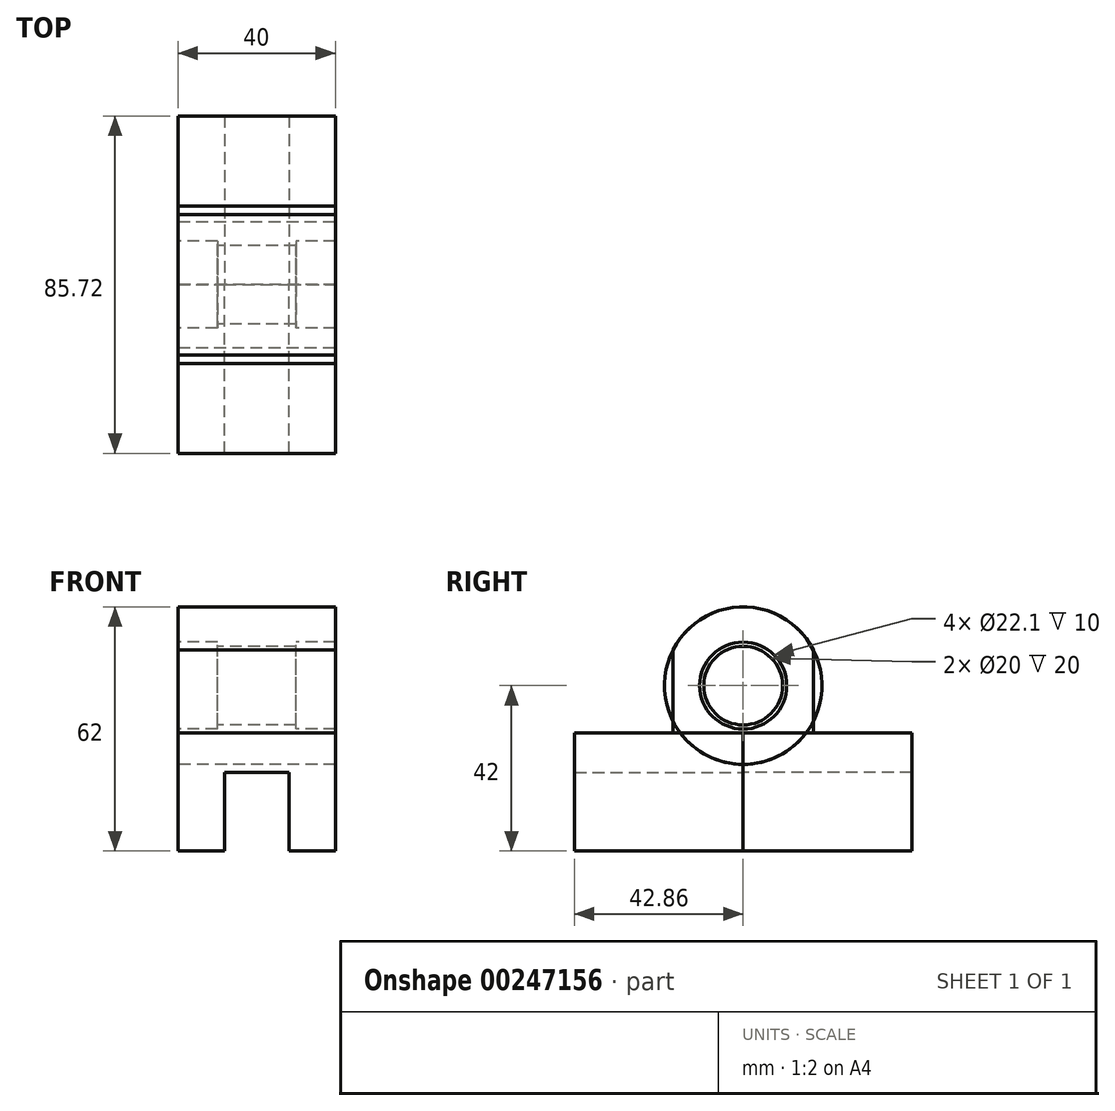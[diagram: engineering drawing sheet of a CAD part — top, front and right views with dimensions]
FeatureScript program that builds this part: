
annotation { "Feature Type Name" : "Feature", "Feature Type Description" : "" }
export const myFeature = defineFeature(function(context is Context, id is Id, definition is map)
    precondition{}
    {
        {
            var Q0;
            Q0=qCreatedBy(makeId("Right.planeOp"),FACE);
            var sketch = newSketch(context, id + "F0", { "sketchPlane" : qUnion([Q0])});
            skCircle(sketch, "E0", {"center": v(0, 0) * mm, "radius": 11.05 * mm});
            skCircle(sketch, "E1", {"center": v(0, 0) * mm, "radius": 20 * mm});
            skCircle(sketch, "E2", {"center": v(0, 0) * mm, "radius": 10 * mm});
            skLineSegment(sketch, "E3.bottom", {"start": v(-17.86, 9) * mm, "end": v(-42.86, 9) * mm});
            skLineSegment(sketch, "E3.top", {"start": v(-17.86, -12) * mm, "end": v(-42.86, -12) * mm});
            skLineSegment(sketch, "E3.left", {"start": v(-17.86, 9) * mm, "end": v(-17.86, -12) * mm});
            skLineSegment(sketch, "E3.right", {"start": v(-42.86, 9) * mm, "end": v(-42.86, -12) * mm});
            skCircle(sketch, "E4", {"center": v(-32.86, 0) * mm, "radius": 3.15 * mm});
            skLineSegment(sketch, "E5.bottom", {"start": v(-42.86, -12) * mm, "end": v(0, -12) * mm});
            skLineSegment(sketch, "E5.top", {"start": v(-42.86, -42) * mm, "end": v(0, -42) * mm});
            skLineSegment(sketch, "E5.left", {"start": v(-42.86, -12) * mm, "end": v(-42.86, -42) * mm});
            skLineSegment(sketch, "E5.right", {"start": v(0, -12) * mm, "end": v(0, -42) * mm});
            skSolve(sketch);
        }
        {
            var Q0;
            Q0=makeQuery(id+"F0.imprint","IMPRINT",FACE,{"disambiguationData":[TD([[makeQuery(id+"F0.imprint","IMPRINT",EDGE,{"derivedFrom":sQuery(id+"F0.wireOp",EDGE,"E0")}),-1.0]])]});
            var Q1;
            {var subQ0=sQuery(id+"F0.wireOp",EDGE,"E5.bottom");var subQ1=sQuery(id+"F0.wireOp",EDGE,"E1");var subQ2=makeQuery(id+"F0.imprint","INTERSECT",VERTEX,{"derivedFrom":[subQ1,subQ0]});Q1=makeQuery(id+"F0.imprint","IMPRINT",FACE,{"disambiguationData":[TD([[makeQuery(id+"F0.imprint","IMPRINT",EDGE,{"disambiguationData":[TD([[subQ2,1.0]])],"derivedFrom":subQ1}),-1.0]])]});}
            extrude(context, id + "F1", {"entities" : qUnion([Q0, Q1]), "depth" : 20 * mm, "offsetDistance" : 25 * mm, "hasSecondDirection" : true, "secondDirectionOppositeDirection" : true, "secondDirectionDepth" : 20 * mm});
        }
        {
            var Q0;
            Q0=makeQuery(id+"F0.imprint","IMPRINT",FACE,{"disambiguationData":[TD([[makeQuery(id+"F0.imprint","IMPRINT",EDGE,{"derivedFrom":sQuery(id+"F0.wireOp",EDGE,"E0")}),1.0]])]});
            extrude(context, id + "F2", {"entities" : qUnion([Q0]), "operationType" : NewBodyOperationType.ADD, "depth" : 10 * mm, "offsetDistance" : 25 * mm, "hasSecondDirection" : true, "secondDirectionOppositeDirection" : true, "secondDirectionDepth" : 10 * mm});
        }
        {
            var Q0;
            Q0=makeQuery(id+"F1.opExtrude","SWEPT_BODY",BODY,{"disambiguationData":[OSD([sQuery(id+"F0.wireOp",EDGE,"E0"),sQuery(id+"F0.wireOp",EDGE,"E1"),sQuery(id+"F0.wireOp",EDGE,"E3.left"),sQuery(id+"F0.wireOp",EDGE,"E5.bottom"),sQuery(id+"F0.wireOp",EDGE,"E5.right")])]});
            var Q1;
            Q1=qCreatedBy(makeId("Front.planeOp"),FACE);
            mirror(context, id + "F3", {"entities" : qUnion([Q0]), "mirrorPlane" : qUnion([Q1])});
        }
        {
            var Q0;
            {var subQ1=sQuery(id+"F0.wireOp",EDGE,"E3.top");Q0=makeQuery(id+"F0.imprint","IMPRINT",FACE,{"disambiguationData":[TD([[makeQuery(id+"F0.imprint","IMPRINT",EDGE,{"derivedFrom":subQ1}),1.0]])]});}
            extrude(context, id + "F4", {"entities" : qUnion([Q0]), "oppositeDirection" : true, "depth" : 20 * mm, "offsetDistance" : 25 * mm, "hasSecondDirection" : true, "secondDirectionOppositeDirection" : false, "secondDirectionDepth" : 20 * mm});
        }
        {
            var Q0;
            Q0=makeQuery(id+"F4.opExtrude","SWEPT_FACE",FACE,{"disambiguationData":[OSD([sQuery(id+"F0.wireOp",EDGE,"E5.top")])]});
            var sketch = newSketch(context, id + "F5", { "sketchPlane" : qUnion([Q0])});
            skLineSegment(sketch, "E6.bottom", {"start": v(-8.2, 42.86) * mm, "end": v(8.2, 42.86) * mm});
            skLineSegment(sketch, "E6.top", {"start": v(-8.2, -1.14) * mm, "end": v(8.2, -1.14) * mm});
            skLineSegment(sketch, "E6.left", {"start": v(-8.2, 42.86) * mm, "end": v(-8.2, -1.14) * mm});
            skLineSegment(sketch, "E6.right", {"start": v(8.2, 42.86) * mm, "end": v(8.2, -1.14) * mm});
            skPoint(sketch, "E6.middle", {"position": v(0, 20.86) * mm});
            skSolve(sketch);
        }
        {
            var Q0;
            {var subQ0=sQuery(id+"F5.wireOp",EDGE,"E6.bottom");Q0=makeQuery(id+"F5.imprint","IMPRINT",FACE,{"disambiguationData":[TD([[makeQuery(id+"F5.imprint","IMPRINT",EDGE,{"derivedFrom":subQ0}),-1.0]])]});}
            extrude(context, id + "F6", {"entities" : qUnion([Q0]), "operationType" : NewBodyOperationType.REMOVE, "oppositeDirection" : true, "depth" : 20 * mm, "offsetDistance" : 25 * mm});
        }
        {
            var Q0;
            Q0=makeQuery(id+"F4.opExtrude","SWEPT_BODY",BODY,{"disambiguationData":[OSD([sQuery(id+"F0.wireOp",EDGE,"E1"),sQuery(id+"F0.wireOp",EDGE,"E3.top"),sQuery(id+"F0.wireOp",EDGE,"E5.bottom"),sQuery(id+"F0.wireOp",EDGE,"E5.top"),sQuery(id+"F0.wireOp",EDGE,"E5.left"),sQuery(id+"F0.wireOp",EDGE,"E5.right")])]});
            var Q1;
            Q1=makeQuery(id+"F4.opExtrude","SWEPT_BODY",BODY,{"disambiguationData":[OSD([sQuery(id+"F0.wireOp",EDGE,"E1"),sQuery(id+"F0.wireOp",EDGE,"E3.top"),sQuery(id+"F0.wireOp",EDGE,"E5.bottom"),sQuery(id+"F0.wireOp",EDGE,"E5.top"),sQuery(id+"F0.wireOp",EDGE,"E5.left"),sQuery(id+"F0.wireOp",EDGE,"E5.right")])]});
            var Q2;
            Q2=qCreatedBy(makeId("Front.planeOp"),FACE);
            mirror(context, id + "F7", {"entities" : qUnion([Q0, Q1]), "mirrorPlane" : qUnion([Q2])});
        }
    });
